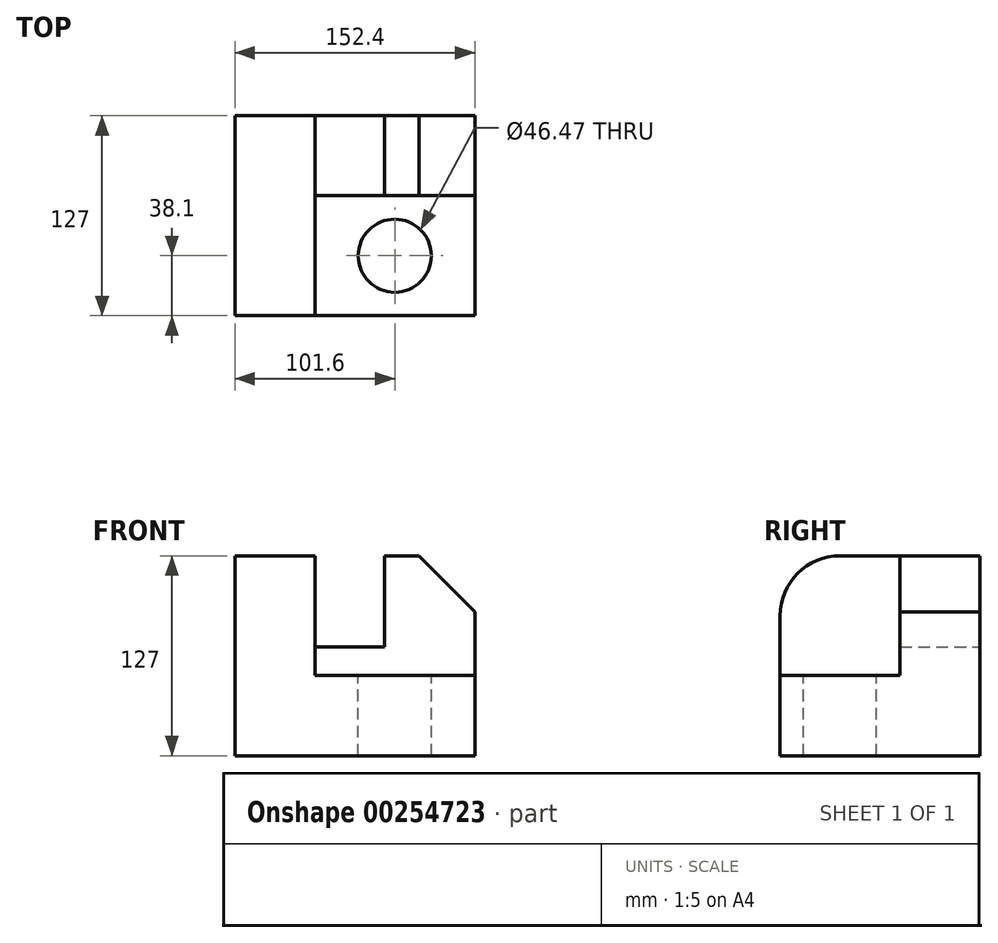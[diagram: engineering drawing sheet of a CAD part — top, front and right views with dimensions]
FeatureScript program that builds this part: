
annotation { "Feature Type Name" : "Feature", "Feature Type Description" : "" }
export const myFeature = defineFeature(function(context is Context, id is Id, definition is map)
    precondition{}
    {
        {
            var Q0;
            Q0=qCreatedBy(makeId("Front.planeOp"),FACE);
            var sketch = newSketch(context, id + "F0", { "sketchPlane" : qUnion([Q0])});
            skLineSegment(sketch, "E0.bottom", {"start": v(76.2, 63.5) * mm, "end": v(-76.2, 63.5) * mm});
            skLineSegment(sketch, "E0.top", {"start": v(76.2, -63.5) * mm, "end": v(-76.2, -63.5) * mm});
            skLineSegment(sketch, "E0.left", {"start": v(76.2, 63.5) * mm, "end": v(76.2, -63.5) * mm});
            skLineSegment(sketch, "E0.right", {"start": v(-76.2, 63.5) * mm, "end": v(-76.2, -63.5) * mm});
            skPoint(sketch, "E0.middle", {"position": v(0, 0) * mm});
            skSolve(sketch);
        }
        {
            var Q0;
            Q0 = qSketchRegion(id + "F0", true);
            extrude(context, id + "F1", {"entities" : qUnion([Q0]), "depth" : 127 * mm});
        }
        {
            var Q0;
            Q0=makeQuery(id+"F1.opExtrude","SWEPT_FACE",FACE,{"disambiguationData":[OSD([sQuery(id+"F0.wireOp",EDGE,"E0.bottom")])]});
            var sketch = newSketch(context, id + "F2", { "sketchPlane" : qUnion([Q0])});
            skLineSegment(sketch, "E1", {"start": v(-25.4, -127) * mm, "end": v(-25.4, -50.8) * mm});
            skPoint(sketch, "E2.end.orphan", {"position": v(-76.2, -51.56) * mm});
            skLineSegment(sketch, "E3", {"start": v(-25.4, -50.8) * mm, "end": v(76.2, -50.8) * mm});
            skSolve(sketch);
        }
        {
            var Q0;
            Q0 = qSketchRegion(id + "F2", true);
            var Q1;
            {var subQ0=sQuery(id+"F2.wireOp",EDGE,"E1");Q1=makeQuery(id+"F2.imprint","IMPRINT",FACE,{"disambiguationData":[TD([[makeQuery(id+"F2.imprint","IMPRINT",EDGE,{"derivedFrom":subQ0}),-1.0]])]});}
            extrude(context, id + "F3", {"entities" : qUnion([Q0, Q1]), "operationType" : NewBodyOperationType.REMOVE, "oppositeDirection" : true, "depth" : 75.95 * mm});
        }
        {
            var Q0;
            Q0=makeQuery(id+"F3.boolean.opBoolean","COPY",FACE,{"derivedFrom":makeQuery(id+"F3.opExtrude","CAP_FACE",FACE,{"disambiguationData":[OSD([sQuery(id+"F0.wireOp",EDGE,"E0.bottom"),sQuery(id+"F0.wireOp",EDGE,"E0.left"),sQuery(id+"F2.wireOp",EDGE,"E1"),sQuery(id+"F2.wireOp",EDGE,"E3")])],"isStart":false})});
            var sketch = newSketch(context, id + "F4", { "sketchPlane" : qUnion([Q0])});
            skPoint(sketch, "E4.orphan", {"position": v(-25.4, -88.9) * mm});
            skPoint(sketch, "E5.end.orphan", {"position": v(76.2, -88.9) * mm});
            skPoint(sketch, "E6.center.orphan", {"position": v(25.4, -88.9) * mm});
            skCircle(sketch, "E7", {"center": v(25.4, -88.9) * mm, "radius": 23.24 * mm});
            skSolve(sketch);
        }
        {
            var Q0;
            Q0=makeQuery(id+"F4.imprint","IMPRINT",FACE,{"disambiguationData":[TD([[makeQuery(id+"F4.imprint","IMPRINT",EDGE,{"derivedFrom":sQuery(id+"F4.wireOp",EDGE,"b310b1dd-2eb9-4b89-9b74-a7011b47f91f0.MirrorC")}),-1.0]])]});
            var Q1;
            Q1=makeQuery(id+"F4.imprint","IMPRINT",FACE,{"disambiguationData":[TD([[makeQuery(id+"F4.imprint","IMPRINT",EDGE,{"derivedFrom":sQuery(id+"F4.wireOp",EDGE,"E7")}),1.0]])]});
            extrude(context, id + "F5", {"entities" : qUnion([Q0, Q1]), "operationType" : NewBodyOperationType.REMOVE, "oppositeDirection" : true, "depth" : 177.8 * mm});
        }
        {
            var Q0;
            Q0=makeQuery(id+"F1.opExtrude","CAP_EDGE",EDGE,{"disambiguationData":[OSD([sQuery(id+"F0.wireOp",EDGE,"E0.bottom")])],"isStart":false});
            fillet(context, id + "F6", {"entities" : qUnion([Q0]), "radius" : 38.1 * mm, "tangentPropagation" : true, "allowEdgeOverflow" : false});
        }
        {
            var Q0;
            Q0=makeQuery(id+"F1.opExtrude","SWEPT_EDGE",EDGE,{"disambiguationData":[OSD([sQuery(id+"F0.wireOp",EDGE,"E0.bottom"),sQuery(id+"F0.wireOp",EDGE,"E0.left")])]});
            chamfer(context, id + "F7", {"entities" : qUnion([Q0]), "width" : 35.56 * mm, "tangentPropagation" : true});
        }
        {
            var Q0;
            Q0=makeQuery(id+"F1.opExtrude","SWEPT_FACE",FACE,{"disambiguationData":[OSD([sQuery(id+"F0.wireOp",EDGE,"E0.bottom")])]});
            var sketch = newSketch(context, id + "F8", { "sketchPlane" : qUnion([Q0])});
            skLineSegment(sketch, "E8", {"start": v(-25.4, -50.8) * mm, "end": v(-25.4, 0) * mm});
            skLineSegment(sketch, "E9", {"start": v(18.85, -50.8) * mm, "end": v(18.85, 0) * mm});
            skSolve(sketch);
        }
        {
            var Q0;
            Q0 = qSketchRegion(id + "F8", true);
            var Q1;
            {var subQ0=sQuery(id+"F8.wireOp",EDGE,"E8");Q1=makeQuery(id+"F8.imprint","IMPRINT",FACE,{"disambiguationData":[TD([[makeQuery(id+"F8.imprint","IMPRINT",EDGE,{"derivedFrom":subQ0}),-1.0]])]});}
            extrude(context, id + "F9", {"entities" : qUnion([Q0, Q1]), "operationType" : NewBodyOperationType.REMOVE, "oppositeDirection" : true, "depth" : 57.9 * mm});
        }
    });
